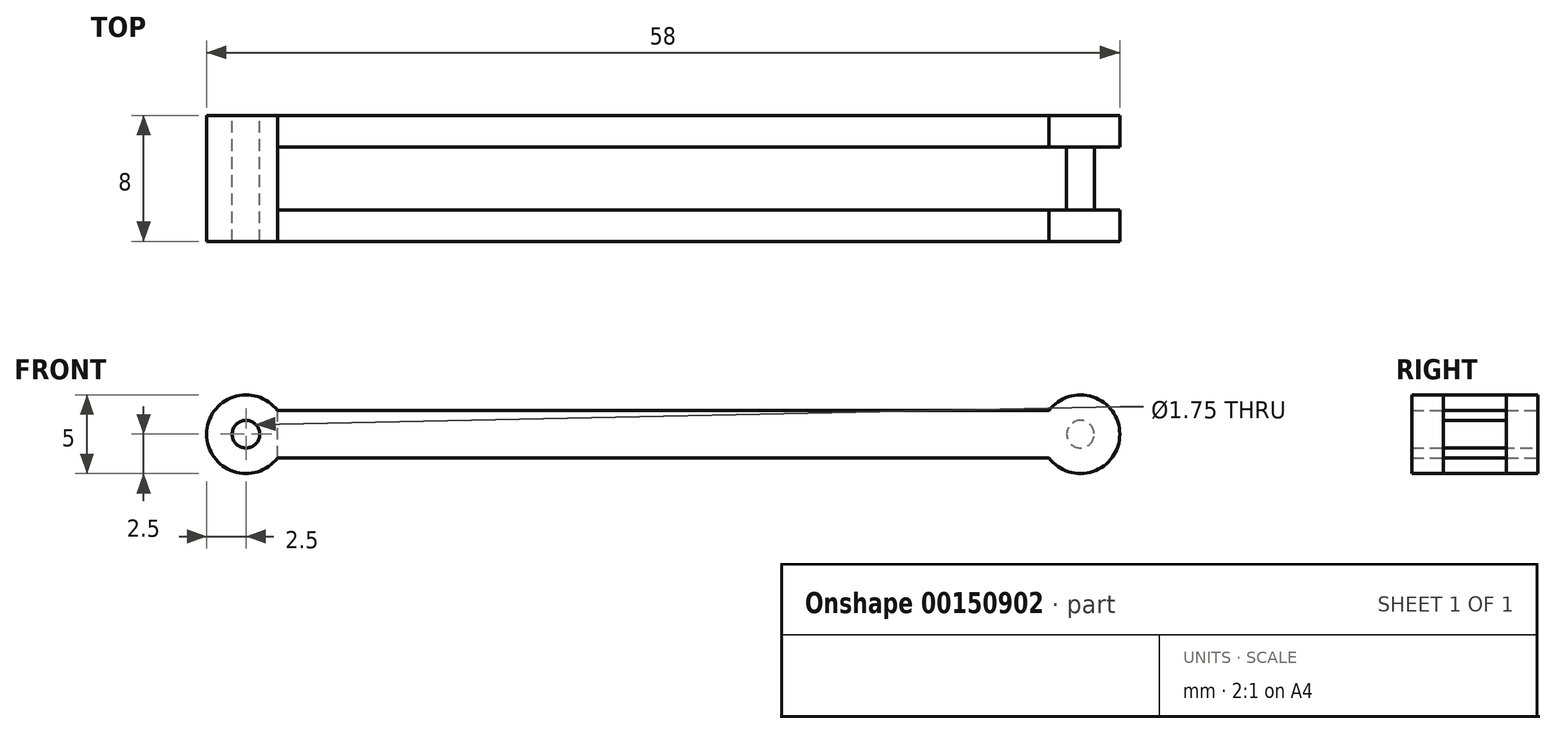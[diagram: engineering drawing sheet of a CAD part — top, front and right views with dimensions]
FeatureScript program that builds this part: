
annotation { "Feature Type Name" : "Feature", "Feature Type Description" : "" }
export const myFeature = defineFeature(function(context is Context, id is Id, definition is map)
    precondition{}
    {
        {
            var Q0;
            Q0=qCreatedBy(makeId("Front.planeOp"),FACE);
            var sketch = newSketch(context, id + "F0", { "sketchPlane" : qUnion([Q0])});
            skCircle(sketch, "E0", {"center": v(-25, 0) * mm, "radius": 0.87 * mm});
            skCircle(sketch, "E1", {"center": v(28, 0) * mm, "radius": 0.87 * mm});
            skLineSegment(sketch, "E2.bottom", {"start": v(-23, -1.5) * mm, "end": v(26, -1.5) * mm});
            skLineSegment(sketch, "E2.top", {"start": v(-23, 1.5) * mm, "end": v(26, 1.5) * mm});
            skArc(sketch, "E3", {"start": v(-23, 1.5) * mm, "mid": v(-27.5, 0) * mm, "end": v(-23, -1.5) * mm});
            skArc(sketch, "E4", {"start": v(26, -1.5) * mm, "mid": v(30.5, 0) * mm, "end": v(26, 1.5) * mm});
            skSolve(sketch);
        }
        {
            var Q0;
            Q0=makeQuery(id+"F0.imprint","IMPRINT",FACE,{"disambiguationData":[TD([[makeQuery(id+"F0.imprint","IMPRINT",EDGE,{"derivedFrom":sQuery(id+"F0.wireOp",EDGE,"E0")}),-1.0]])]});
            extrude(context, id + "F1", {"entities" : qUnion([Q0]), "endBound" : BoundingType.SYMMETRIC, "depth" : 8 * mm});
        }
        {
            var Q0;
            Q0=qCreatedBy(makeId("Front.planeOp"),FACE);
            var sketch = newSketch(context, id + "F2", { "sketchPlane" : qUnion([Q0])});
            skCircle(sketch, "E5", {"center": v(28, 0) * mm, "radius": 2.5 * mm});
            skArc(sketch, "E6.0", {"start": v(26, -1.5) * mm, "mid": v(30.5, 0) * mm, "end": v(26, 1.5) * mm});
            skSolve(sketch);
        }
        {
            var Q0;
            Q0=qSketchRegion(id+"F2",true);
            extrude(context, id + "F3", {"entities" : qUnion([Q0]), "operationType" : NewBodyOperationType.REMOVE, "endBound" : BoundingType.SYMMETRIC, "oppositeDirection" : true, "depth" : 4 * mm});
        }
        {
            var Q0;
            Q0=makeQuery(id+"F0.imprint","IMPRINT",FACE,{"disambiguationData":[TD([[makeQuery(id+"F0.imprint","IMPRINT",EDGE,{"derivedFrom":sQuery(id+"F0.wireOp",EDGE,"E1")}),1.0]])]});
            extrude(context, id + "F4", {"entities" : qUnion([Q0]), "operationType" : NewBodyOperationType.ADD, "endBound" : BoundingType.SYMMETRIC, "depth" : 8 * mm});
        }
        {
            var Q0;
            Q0=qCreatedBy(makeId("Top.planeOp"),FACE);
            var sketch = newSketch(context, id + "F5", { "sketchPlane" : qUnion([Q0])});
            skLineSegment(sketch, "E7.bottom", {"start": v(26, -2) * mm, "end": v(-23, -2) * mm});
            skLineSegment(sketch, "E7.top", {"start": v(26, 2) * mm, "end": v(-23, 2) * mm});
            skLineSegment(sketch, "E7.left", {"start": v(26, -2) * mm, "end": v(26, 2) * mm});
            skLineSegment(sketch, "E7.right", {"start": v(-23, -2) * mm, "end": v(-23, 2) * mm});
            skSolve(sketch);
        }
        {
            var Q0;
            Q0=qSketchRegion(id+"F5",true);
            extrude(context, id + "F6", {"entities" : qUnion([Q0]), "operationType" : NewBodyOperationType.REMOVE, "endBound" : BoundingType.SYMMETRIC, "oppositeDirection" : true, "depth" : 5 * mm});
        }
    });
